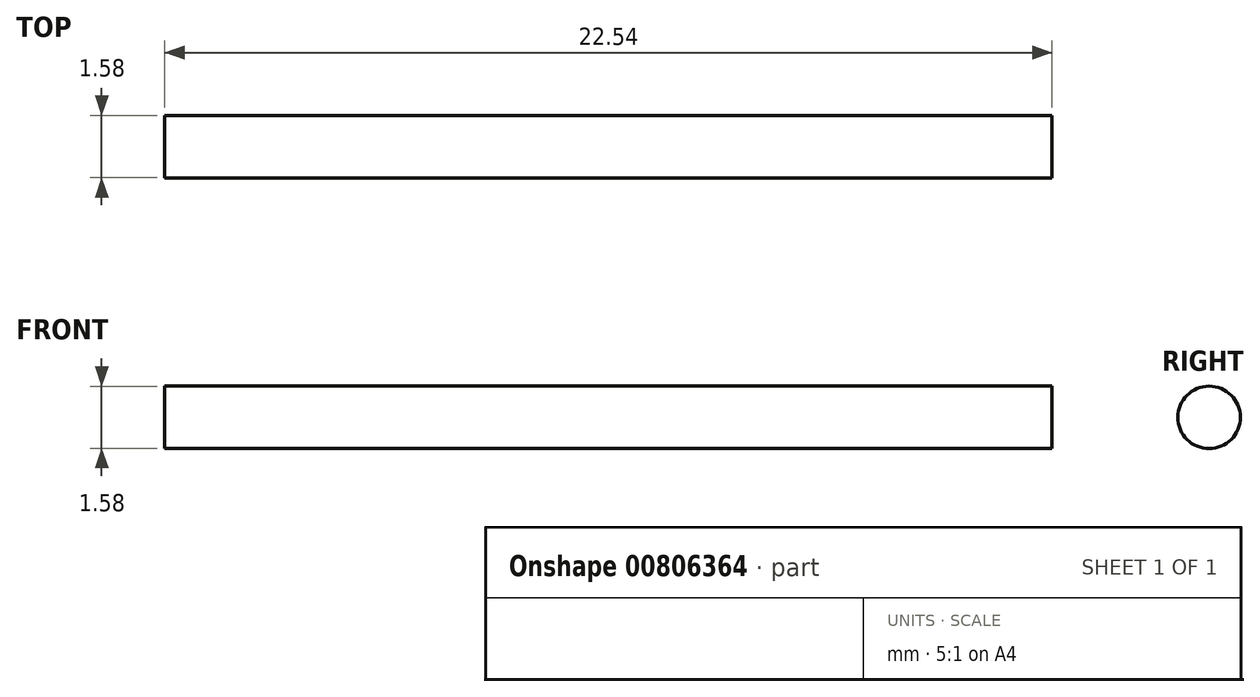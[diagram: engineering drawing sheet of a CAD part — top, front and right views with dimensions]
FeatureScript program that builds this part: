
annotation { "Feature Type Name" : "Feature", "Feature Type Description" : "" }
export const myFeature = defineFeature(function(context is Context, id is Id, definition is map)
    precondition{}
    {
        {
            var Q0;
            Q0=qCreatedBy(makeId("Right.planeOp"),FACE);
            var sketch = newSketch(context, id + "F0", { "sketchPlane" : qUnion([Q0])});
            skCircle(sketch, "E0", {"center": v(0, 0) * mm, "radius": 0.8 * mm});
            skSolve(sketch);
        }
        {
            var Q0;
            Q0 = qSketchRegion(id + "F0", true);
            extrude(context, id + "F1", {"entities" : qUnion([Q0]), "depth" : 22.54 * mm, "offsetDistance" : 25.4 * mm});
        }
    });
